# Revit family: ADLR-410-xxx-DPOx
name_source: partatom
category: Leuchten
units: mm (PartAtom-declared; Revit-internal decimal feet)

## family parameters
Basisbauteil = Fläche
Beim Laden mit Abzugskörper schneiden = Nein
Bemaßung runder Anschluss = Durchmesser verwenden
Gemeinsam genutzt = Nein
Lichtquelle = Ja
OmniClass-Nummer = 23.80.70.11
OmniClass-Titel = Luminaries for Internal Lighting
Raumberechnungspunkt = Nein
Teiletyp = Normal

## types (9) — shared parameters
Baugruppenkennzeichen = D5020200
Datei für fotometrisches Netz = ADLR 4105000840 DPO.IES
Emissionsform beim Rendern sichtbar = Nein
Farbfilter = 16777215
Farbtemperaturverschiebung bei Dämpfen der Lampe = <Keine Auswahl>
Hersteller = RIDI Leuchten GmbH
Lampe = LED
Neigungswinkel = 90.00°
URL = www.ridi.de
Von Kreisdurchmesser aussenden = 361 mm  [stored 1.18438 ft]
brand = RIDI
conformity mark = CE
electrical safety class = 1
height = 68 mm
ingress protection (IP) code = IP40
length = 410 mm  [stored 1.34514 ft]
nominal frequency = 50-60Hz
nominal voltage = 230
voltage type (AC, DC, UC) = AC
weight = 4.57 kg
width = 410 mm  [stored 1.34514 ft]
zero-valued in all types: Vorgabe-Ansicht

## per-type parameters (varying)
| type | Modell | Scheinlast | product name | rated input power |
| ADLR 410/5000-840 DPO | 0321242 | 30 VA | ADLR 410/5000-840 DPO | 30 |
| ADLR 410/5000-840 DPO-DALI | 0331242 | 30 VA | ADLR 410/5000-840 DPO-DALI | 30 |
| ADLR 410/6000-840 DPO | 0321246 | 37 VA | ADLR 410/6000-840 DPO | 37 |
| ADLR 410/6000-840 DPO-DALI | 0331246 | 37 VA | ADLR 410/6000-840 DPO-DALI | 37 |
| ADLR 410/5000-830 DPO | 0326720 | 30 VA | ADLR 410/5000-830 DPO | 30 |
| ADLR 410/5000-830 DPO-DALI | 0336720 | 30 VA | ADLR 410/5000-830 DPO-DALI | 30 |
| ADLR 410/6000-830 DPO | 0326724 | 37 VA | ADLR 410/6000-830 DPO | 37 |
| ADLR 410/6000-830 DPO-DALI | 0336724 | 37 VA | ADLR 410/6000-830 DPO | 37 |
| ADLR 410/6000-8TW DPO | 0336765 | 41 VA | ADLR 410/6000-8TW DPO | 41 |

note: [stored X ft] marks values corroborated as IEEE doubles in the binary element streams (Revit-internal decimal feet)
